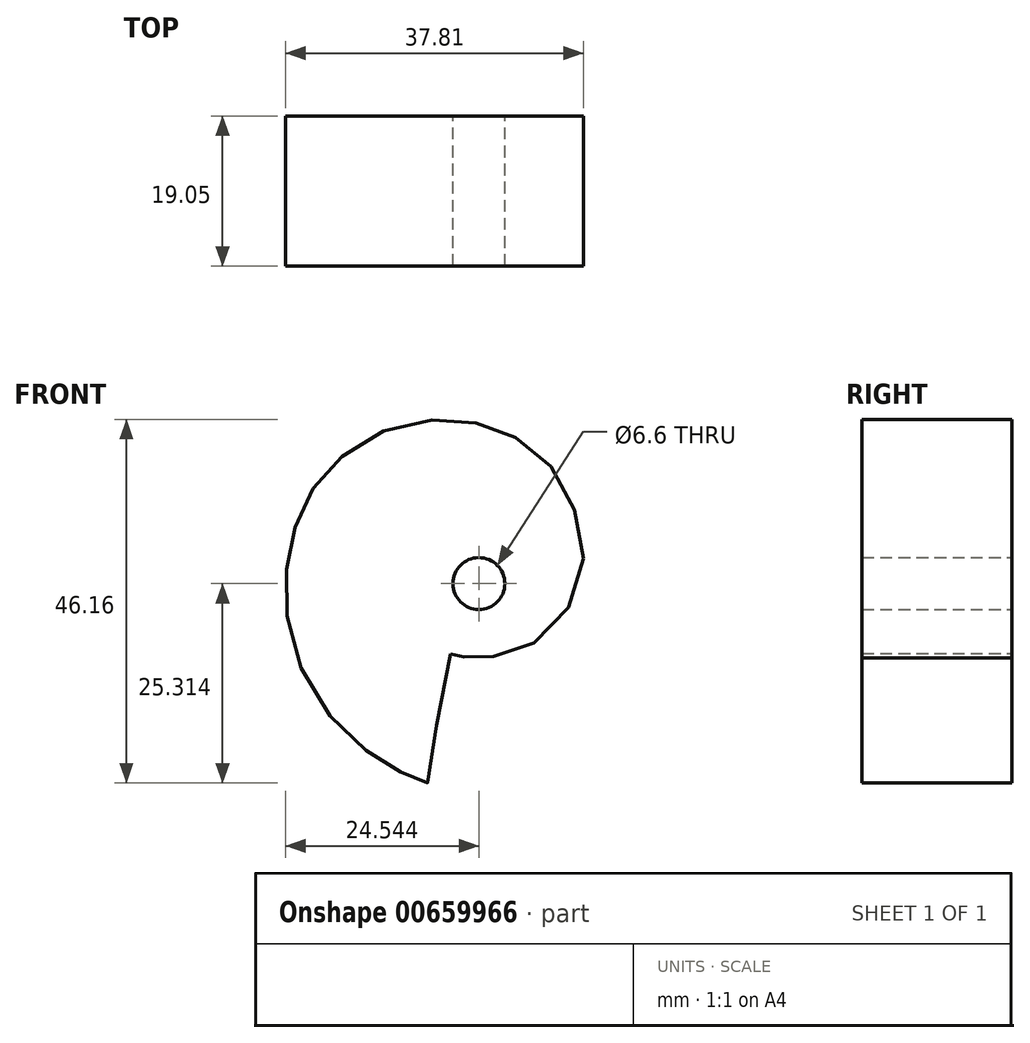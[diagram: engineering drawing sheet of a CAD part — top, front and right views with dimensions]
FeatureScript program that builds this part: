
annotation { "Feature Type Name" : "Feature", "Feature Type Description" : "" }
export const myFeature = defineFeature(function(context is Context, id is Id, definition is map)
    precondition{}
    {
        {
            var Q0;
            Q0=qCreatedBy(makeId("Front.planeOp"),FACE);
            var sketch = newSketch(context, id + "F0", { "sketchPlane" : qUnion([Q0])});
            skFitSpline(sketch, "E0", {"points": [v(1.26, -24.18) * mm, v(-1.58, -40.52) * mm, v(-1.63, -40.56) * mm, v(-3.42, -39.91) * mm, v(-7.48, -37.83) * mm, v(-13.1, -33.24) * mm, v(-18.35, -24.45) * mm, v(-19.69, -15.94) * mm, v(-18.98, -9.73) * mm, v(-16.7, -3.99) * mm, v(-12.8, 0.63) * mm, v(-6.04, 4.61) * mm, v(1.71, 5.54) * mm, v(7.19, 4.33) * mm, v(12.87, 0.92) * mm, v(17, -5.84) * mm, v(17.92, -13.8) * mm, v(13.8, -21.34) * mm, v(7.9, -24.32) * mm, v(3.84, -24.68) * mm, v(2.33, -24.46) * mm, v(1.53, -24.3) * mm, v(1.44, -24.25) * mm, v(1.26, -24.18) * mm]});
            skCircle(sketch, "E1", {"center": v(4.85, -15.26) * mm, "radius": 3.3 * mm});
            skSolve(sketch);
        }
        {
            var Q0;
            Q0=qSketchRegion(id+"F0",true);
            extrude(context, id + "F1", {"entities" : qUnion([Q0]), "depth" : 19.05 * mm, "offsetDistance" : 25.4 * mm});
        }
    });
